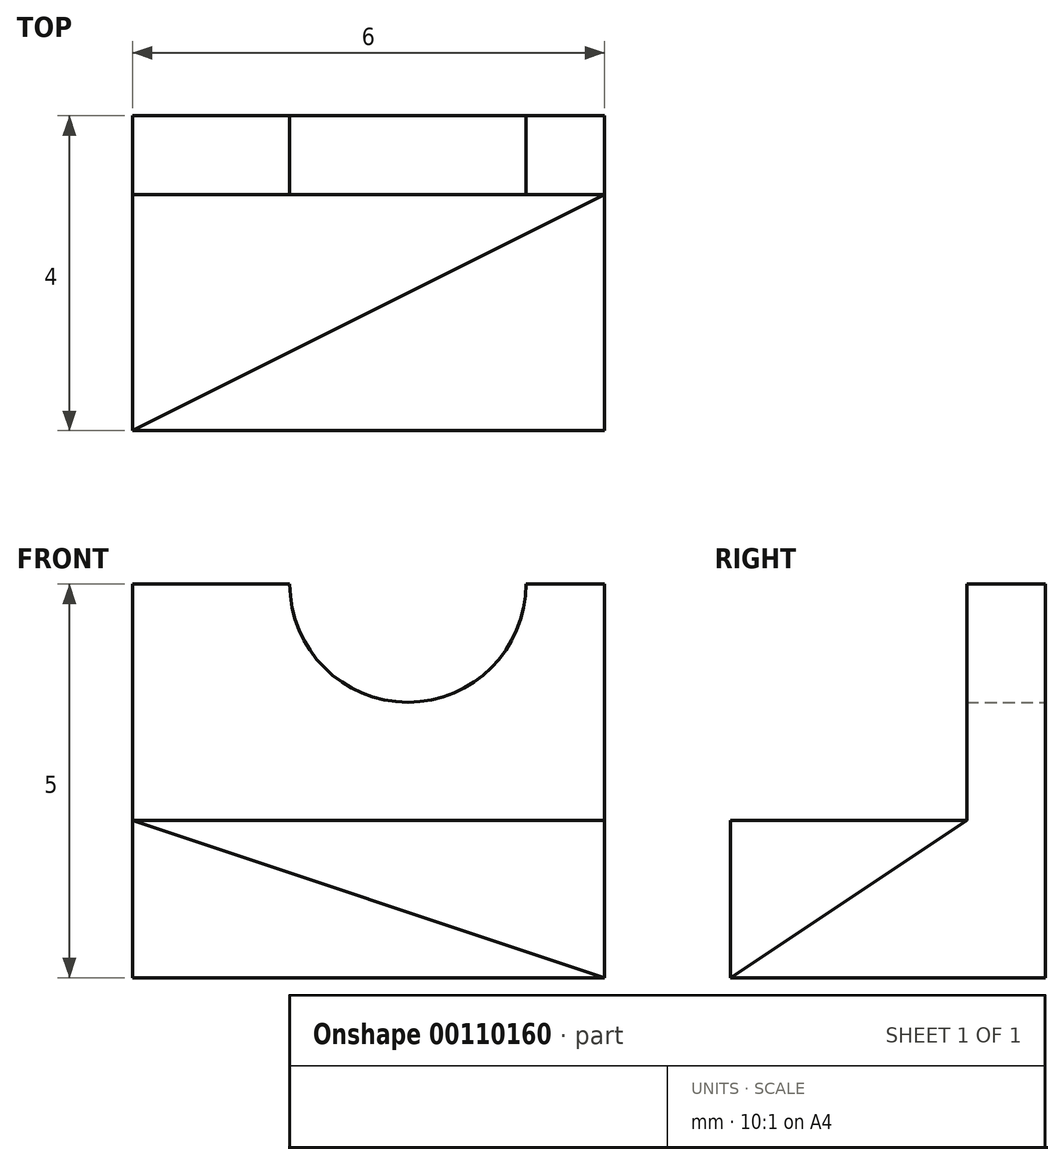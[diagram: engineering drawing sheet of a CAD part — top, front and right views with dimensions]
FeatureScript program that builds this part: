
annotation { "Feature Type Name" : "Feature", "Feature Type Description" : "" }
export const myFeature = defineFeature(function(context is Context, id is Id, definition is map)
    precondition{}
    {
        {
            var Q0;
            Q0=qCreatedBy(makeId("Front.planeOp"),FACE);
            var sketch = newSketch(context, id + "F0", { "sketchPlane" : qUnion([Q0])});
            skLineSegment(sketch, "E0.bottom", {"start": v(0, 0) * mm, "end": v(6, 0) * mm});
            skLineSegment(sketch, "E0.top", {"start": v(0, 5) * mm, "end": v(2, 5) * mm});
            skLineSegment(sketch, "E0.left", {"start": v(0, 0) * mm, "end": v(0, 5) * mm});
            skLineSegment(sketch, "E0.right", {"start": v(6, 0) * mm, "end": v(6, 5) * mm});
            skArc(sketch, "E1", {"start": v(2, 5) * mm, "mid": v(3.5, 3.5) * mm, "end": v(5, 5) * mm});
            skLineSegment(sketch, "E2.trimOffspring", {"start": v(5, 5) * mm, "end": v(6, 5) * mm});
            skSolve(sketch);
        }
        {
            var Q0;
            Q0=makeQuery(id+"F0.imprint","IMPRINT",FACE,{"disambiguationData":[TD([[makeQuery(id+"F0.imprint","IMPRINT",EDGE,{"derivedFrom":sQuery(id+"F0.wireOp",EDGE,"E0.bottom")}),1.0]])]});
            extrude(context, id + "F1", {"entities" : qUnion([Q0]), "depth" : 4 * mm});
        }
        {
            var Q0;
            Q0=makeQuery(id+"F1.opExtrude","CAP_FACE",FACE,{"disambiguationData":[OSD([sQuery(id+"F0.wireOp",EDGE,"E0.bottom"),sQuery(id+"F0.wireOp",EDGE,"E0.top"),sQuery(id+"F0.wireOp",EDGE,"E0.left"),sQuery(id+"F0.wireOp",EDGE,"E0.right"),sQuery(id+"F0.wireOp",EDGE,"E1"),sQuery(id+"F0.wireOp",EDGE,"E2.trimOffspring")])],"isStart":false});
            var sketch = newSketch(context, id + "F2", { "sketchPlane" : qUnion([Q0])});
            skLineSegment(sketch, "E3.bottom", {"start": v(0, 2) * mm, "end": v(6, 2) * mm});
            skLineSegment(sketch, "E3.top", {"start": v(0, 5) * mm, "end": v(6, 5) * mm});
            skLineSegment(sketch, "E3.left", {"start": v(0, 2) * mm, "end": v(0, 5) * mm});
            skLineSegment(sketch, "E3.right", {"start": v(6, 2) * mm, "end": v(6, 5) * mm});
            skSolve(sketch);
        }
        {
            var Q0;
            Q0 = qSketchRegion(id + "F2", true);
            extrude(context, id + "F3", {"entities" : qUnion([Q0]), "operationType" : NewBodyOperationType.REMOVE, "oppositeDirection" : true, "depth" : 3 * mm});
        }
        {
            var Q0;
            Q0=makeQuery(id+"F3.boolean.opBoolean","COPY",VERTEX,{"derivedFrom":makeQuery(id+"F3.opExtrude","CAP_VERTEX",VERTEX,{"disambiguationData":[OSD([sQuery(id+"F0.wireOp",EDGE,"E0.left"),sQuery(id+"F2.wireOp",EDGE,"E3.bottom"),sQuery(id+"F2.wireOp",EDGE,"E3.left")])],"isStart":true})});
            var Q1;
            Q1=makeQuery(id+"F1.opExtrude","CAP_VERTEX",VERTEX,{"disambiguationData":[OSD([sQuery(id+"F0.wireOp",EDGE,"E0.bottom"),sQuery(id+"F0.wireOp",EDGE,"E0.right")])],"isStart":false});
            var Q2;
            Q2=makeQuery(id+"F3.boolean.opBoolean","COPY",VERTEX,{"derivedFrom":makeQuery(id+"F3.opExtrude","CAP_VERTEX",VERTEX,{"disambiguationData":[OSD([sQuery(id+"F0.wireOp",EDGE,"E0.right"),sQuery(id+"F2.wireOp",EDGE,"E3.bottom"),sQuery(id+"F2.wireOp",EDGE,"E3.right")])],"isStart":false})});
            cPlane(context, id + "F4", {"entities" : qUnion([Q0, Q1, Q2]), "cplaneType" : CPlaneType.THREE_POINT, "offset" : 25 * mm, "width" : 150 * mm, "height" : 150 * mm});
        }
        {
            var Q0;
            Q0=qCreatedBy(id+"F4.planeOp",FACE);
            var sketch = newSketch(context, id + "F5", { "sketchPlane" : qUnion([Q0])});
            skPoint(sketch, "E4.0", {"position": v(-1.04, 2.22) * mm});
            skPoint(sketch, "E4.1", {"position": v(5.19, -0.28) * mm});
            skPoint(sketch, "E4.2", {"position": v(5.19, 3.33) * mm});
            skLineSegment(sketch, "E5", {"start": v(-1.04, 2.22) * mm, "end": v(5.19, -0.28) * mm});
            skLineSegment(sketch, "E6", {"start": v(5.19, -0.28) * mm, "end": v(5.19, 3.33) * mm});
            skLineSegment(sketch, "E7", {"start": v(5.19, 3.33) * mm, "end": v(-1.04, 2.22) * mm});
            skSolve(sketch);
        }
        {
            var Q0;
            Q0 = qSketchRegion(id + "F5", true);
            extrude(context, id + "F6", {"entities" : qUnion([Q0]), "operationType" : NewBodyOperationType.REMOVE, "endBound" : BoundingType.THROUGH_ALL, "oppositeDirection" : true, "depth" : 25 * mm});
        }
    });
